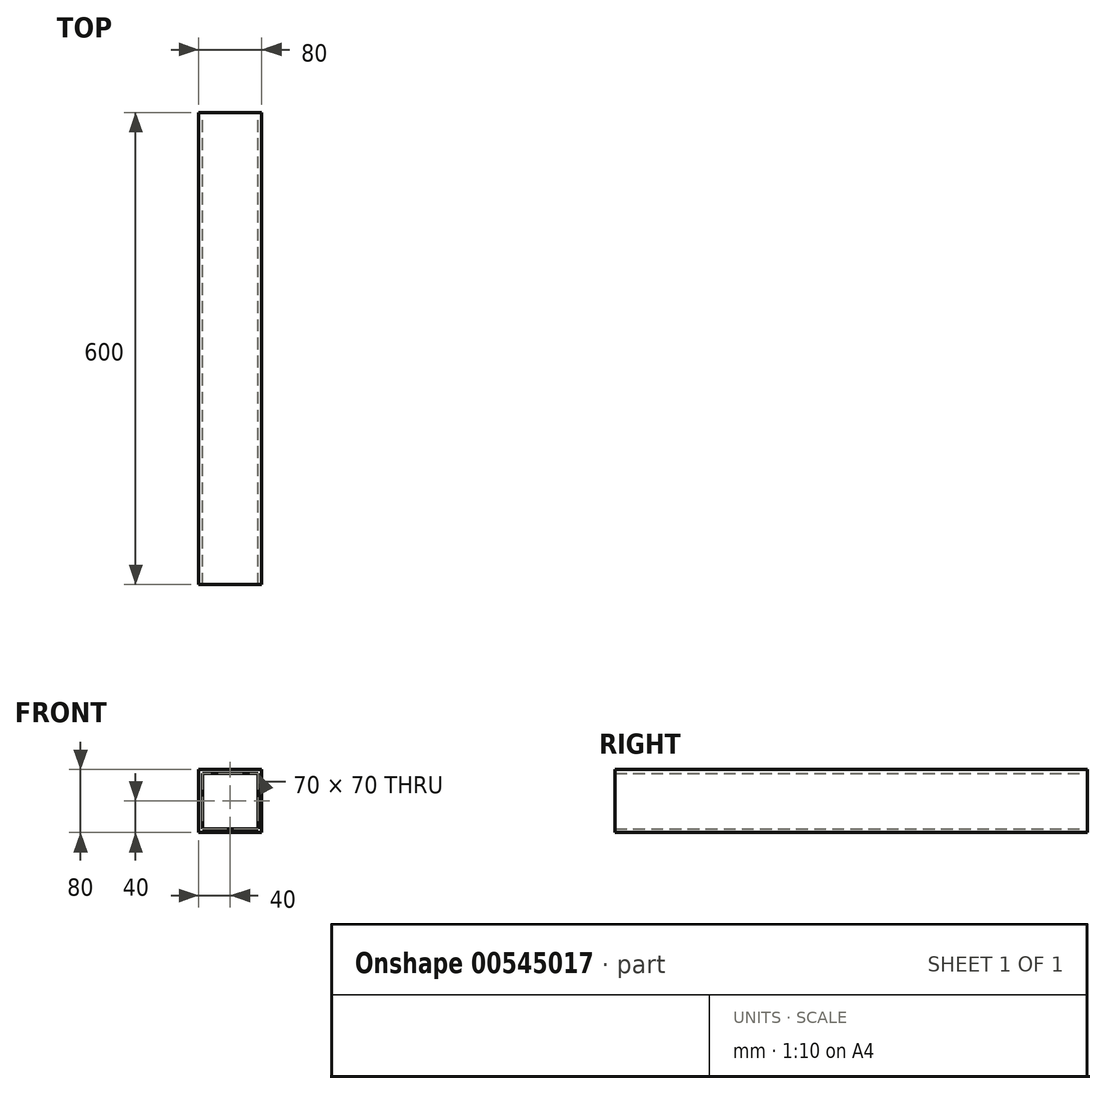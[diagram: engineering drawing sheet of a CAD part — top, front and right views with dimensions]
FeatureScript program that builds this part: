
annotation { "Feature Type Name" : "Feature", "Feature Type Description" : "" }
export const myFeature = defineFeature(function(context is Context, id is Id, definition is map)
    precondition{}
    {
        {
            var Q0;
            Q0=qCreatedBy(makeId("Front.planeOp"),FACE);
            var sketch = newSketch(context, id + "F0", { "sketchPlane" : qUnion([Q0])});
            skLineSegment(sketch, "E0.bottom", {"start": v(-40, 40) * mm, "end": v(40, 40) * mm});
            skLineSegment(sketch, "E0.top", {"start": v(-40, -40) * mm, "end": v(40, -40) * mm});
            skLineSegment(sketch, "E0.left", {"start": v(-40, 40) * mm, "end": v(-40, -40) * mm});
            skLineSegment(sketch, "E0.right", {"start": v(40, 40) * mm, "end": v(40, -40) * mm});
            skPoint(sketch, "E0.middle", {"position": v(0, 0) * mm});
            skLineSegment(sketch, "E1.bottom", {"start": v(35, 35) * mm, "end": v(-35, 35) * mm});
            skLineSegment(sketch, "E1.top", {"start": v(35, -35) * mm, "end": v(-35, -35) * mm});
            skLineSegment(sketch, "E1.left", {"start": v(35, 35) * mm, "end": v(35, -35) * mm});
            skLineSegment(sketch, "E1.right", {"start": v(-35, 35) * mm, "end": v(-35, -35) * mm});
            skSolve(sketch);
        }
        {
            var Q0;
            Q0=makeQuery(id+"F0.imprint","IMPRINT",FACE,{"disambiguationData":[TD([[makeQuery(id+"F0.imprint","IMPRINT",EDGE,{"derivedFrom":sQuery(id+"F0.wireOp",EDGE,"E0.bottom")}),-1.0]])]});
            extrude(context, id + "F1", {"entities" : qUnion([Q0]), "endBound" : BoundingType.SYMMETRIC, "depth" : 600 * mm, "offsetDistance" : 25 * mm});
        }
    });
